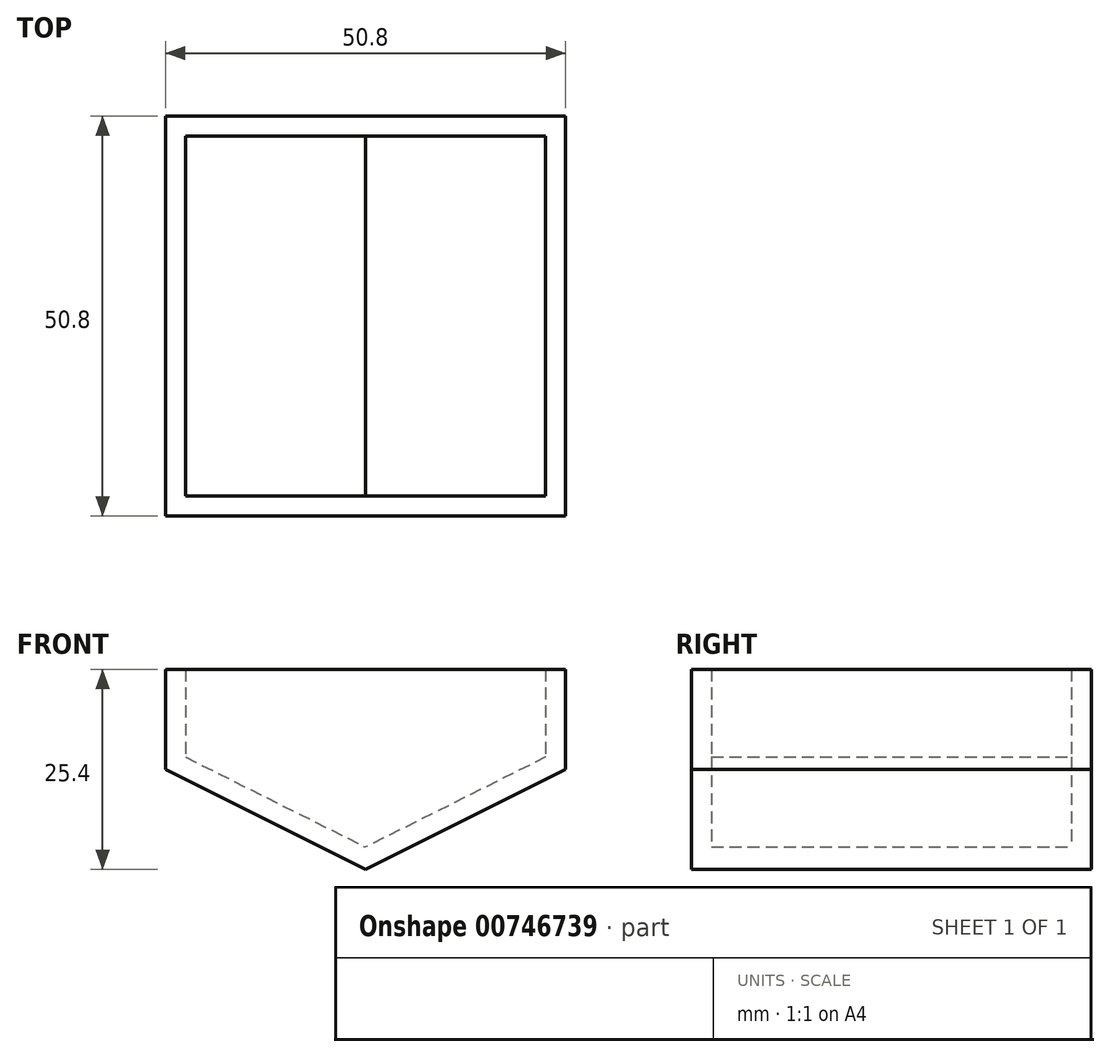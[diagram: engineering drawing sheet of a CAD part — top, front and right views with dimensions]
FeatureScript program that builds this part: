
annotation { "Feature Type Name" : "Feature", "Feature Type Description" : "" }
export const myFeature = defineFeature(function(context is Context, id is Id, definition is map)
    precondition{}
    {
        {
            var Q0;
            Q0=qCreatedBy(makeId("Front.planeOp"),FACE);
            var sketch = newSketch(context, id + "F0", { "sketchPlane" : qUnion([Q0])});
            skLineSegment(sketch, "E0", {"start": v(0, 0) * mm, "end": v(0, 12.7) * mm});
            skLineSegment(sketch, "E1", {"start": v(0, 0) * mm, "end": v(0, -12.7) * mm});
            skLineSegment(sketch, "E2", {"start": v(0, 12.7) * mm, "end": v(-25.4, 12.7) * mm});
            skLineSegment(sketch, "E3", {"start": v(0, 12.7) * mm, "end": v(25.4, 12.7) * mm});
            skLineSegment(sketch, "E4", {"start": v(-25.4, 12.7) * mm, "end": v(-25.4, 0) * mm});
            skLineSegment(sketch, "E5", {"start": v(25.4, 12.7) * mm, "end": v(25.4, 0) * mm});
            skLineSegment(sketch, "E6", {"start": v(25.4, 0) * mm, "end": v(0, -12.7) * mm});
            skLineSegment(sketch, "E7", {"start": v(-25.4, 0) * mm, "end": v(0, -12.7) * mm});
            skSolve(sketch);
        }
        {
            var Q0;
            Q0=makeQuery(id+"F0.imprint","IMPRINT",FACE,{"disambiguationData":[TD([[makeQuery(id+"F0.imprint","IMPRINT",EDGE,{"derivedFrom":sQuery(id+"F0.wireOp",EDGE,"E0")}),1.0]])]});
            var Q1;
            Q1=makeQuery(id+"F0.imprint","IMPRINT",FACE,{"disambiguationData":[TD([[makeQuery(id+"F0.imprint","IMPRINT",EDGE,{"derivedFrom":sQuery(id+"F0.wireOp",EDGE,"E0")}),-1.0]])]});
            extrude(context, id + "F1", {"entities" : qUnion([Q0, Q1]), "depth" : 50.8 * mm, "offsetDistance" : 25.4 * mm});
        }
        {
            var Q0;
            Q0=makeQuery(id+"F1.opExtrude","SWEPT_FACE",FACE,{"disambiguationData":[OSD([sQuery(id+"F0.wireOp",EDGE,"E2"),sQuery(id+"F0.wireOp",EDGE,"E3")])]});
            shell(context, id + "F2", {"entities" : qUnion([Q0]), "thickness" : 2.54 * mm});
        }
    });
